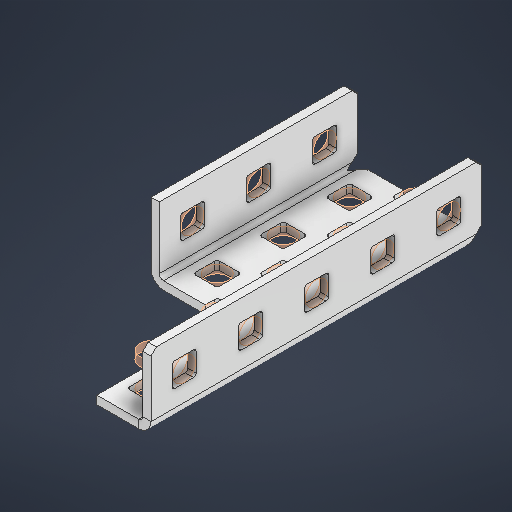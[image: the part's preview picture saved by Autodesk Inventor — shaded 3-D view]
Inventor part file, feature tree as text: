
AUTODESK INVENTOR PART (.ipt)
format: ipt  version: 2025.2 (Build 292293000, 293)  size: 699,904 bytes
history: native  units: in
note: dims shown in document units (in); Inventor stores cm internally (conversion verified against a paired STEP export)
features: other x32, extrude x24, sheet_metal_op x11, sketch x4, pattern_linear x2, mirror x1, chamfer x1
ambient origin geometry x8: Origin, YZ Plane, XZ Plane, XY Plane, X Axis, Y Axis, Z Axis, Center Point
bodies: Solid1 (feature_tree), Body (feature_tree)
feature tree (75):
  sheet_metal_op  "Flanges"
  other  "Flange Pattern Plane"
  other  "Flange Pattern Sketch"
  sheet_metal_op  "Flange Pattern"
  sheet_metal_op  "Body Pattern"
  pattern_linear  "Center Pattern"  Spacing1=0.0312in  [1 undecoded]
  other  "Arc Length"
  mirror  "Notch Mirror"
  pattern_linear  "Notch Pattern"  Spacing1=0.125in  [1 undecoded]
  chamfer  "End Chamfer"
  extrude  "Half Cut"  Depth=0.0625in
  extrude  "Extrusion2"  Depth=0.5in TaperAngle=90.0deg
  other  "Plate1"
  sketch  "Sketch2"  dims[d1=2.5in]
  other  "Plate2"
  sheet_metal_op  "Bend1"
  sheet_metal_op  "Corner1"
  sketch  "Sketch Rectangular Pattern1"  dims[d0=1.0in]
  other  "Srf1"
  other  "Srf2"
  other  "Srf91"
  sheet_metal_op  "Body Pattern Sketch"
  sketch  "Sketch Rectangular Pattern2"  dims[d2=0.0625in]
  other  "Srf92"
  other  "Srf786"
  other  "Srf823"
  other  "Srf824"
  other  "Srf825"
  other  "Srf826"
  other  "Srf827"
  other  "Srf828"
  other  "Srf829"
  other  "Srf856"
  other  "Srf857"
  other  "Srf858"
  other  "Srf859"
  other  "Srf860"
  other  "Srf861"
  other  "Srf862"
  other  "Srf889"
  other  "Srf890"
  other  "Srf891"
  other  "Srf892"
  other  "Srf922"
  other  "Srf959"
  sketch  "Sketch17"  dims[d3=0.0625in d4=0.0312in d5=0.125in d6=0.0625in d7=0.5in d8=90.0deg d9=0.0312in d10=0.25in d11=0.0625in d12=0.0625in d16=0.182in d17=0.02in d18=0.0625in d19=0.0in d20=0.25in d21=0.25in d38=1.9685in d40=0.5in d41=0.7874in d43=1.0in d46=0.172in d47=1.0in d48=0.0in d49=0.182in d50=0.02in d51=0.25in d52=0.25in d53=0.0625in d54=0.0in d55=0.172in d56=1.0in d57=0.0in d58=0.25in d60=1.9685in d62=0.5in d63=0.7874in d65=0.5in d85=0.1473in d86=0.1782in d88=0.04in d89=0.0625in d90=0.0in d91=0.04in d92=0.0491in d95=2.5in d96=0.04in d97=0.25in d98=45.0deg d99=0.25in d100=0.5in d101=0.0in d102=2.497in d106=0.182in d107=0.02in d108=0.5in d109=0.5in d110=0.0625in d111=0.0in d112=0.172in d113=0.5in d114=0.0in d117=0.5in d118=0.5in d119=0.5in d121=1.0in d122=0.59in d123=0.0in]
  sheet_metal_op  "Flange Stamp"
  sheet_metal_op  "Flange Circle"
  sheet_metal_op  "Body Stamp"
  sheet_metal_op  "Body Circle"
  other  "Center Stamp"
  other  "Center Circle"
  sheet_metal_op  "Notch"
  extrude  "ExtrusionSrf2"  Depth=0.59in
  extrude  "ExtrusionSrf92"  Depth=0.0625in
  extrude  "ExtrusionSrf823"  Depth=0.0625in
  extrude  "ExtrusionSrf824"  Depth=0.59in
  extrude  "ExtrusionSrf825"  Depth=0.02in
  extrude  "ExtrusionSrf826"  Depth=0.0625in
  extrude  "ExtrusionSrf827"  TaperAngle=0.0deg  [1 undecoded]
  extrude  "ExtrusionSrf828"  Depth=0.59in
  extrude  "ExtrusionSrf829"  Depth=0.59in
  extrude  "ExtrusionSrf856"  Depth=0.5in
  extrude  "ExtrusionSrf857"  Depth=0.59in
  extrude  "ExtrusionSrf858"  Depth=1.0in TaperAngle=0.0deg
  extrude  "ExtrusionSrf859"  Depth=0.59in
  extrude  "ExtrusionSrf860"  Depth=0.02in
  extrude  "ExtrusionSrf861"  Depth=0.59in
  extrude  "ExtrusionSrf862"  Depth=0.59in
  extrude  "ExtrusionSrf889"  Depth=0.0625in
  extrude  "ExtrusionSrf890"  TaperAngle=0.0deg  [1 undecoded]
  extrude  "ExtrusionSrf891"  Depth=0.59in
  extrude  "ExtrusionSrf892"  Depth=1.0in TaperAngle=0.0deg
  extrude  "ExtrusionSrf922"  Depth=0.59in
  extrude  "ExtrusionSrf959"  Depth=0.59in
note: 4 required parameter values undecoded (feature->parameter linkage not recoverable at this tier; creation-order binding heuristic only, values carry confidence <= 0.55)
